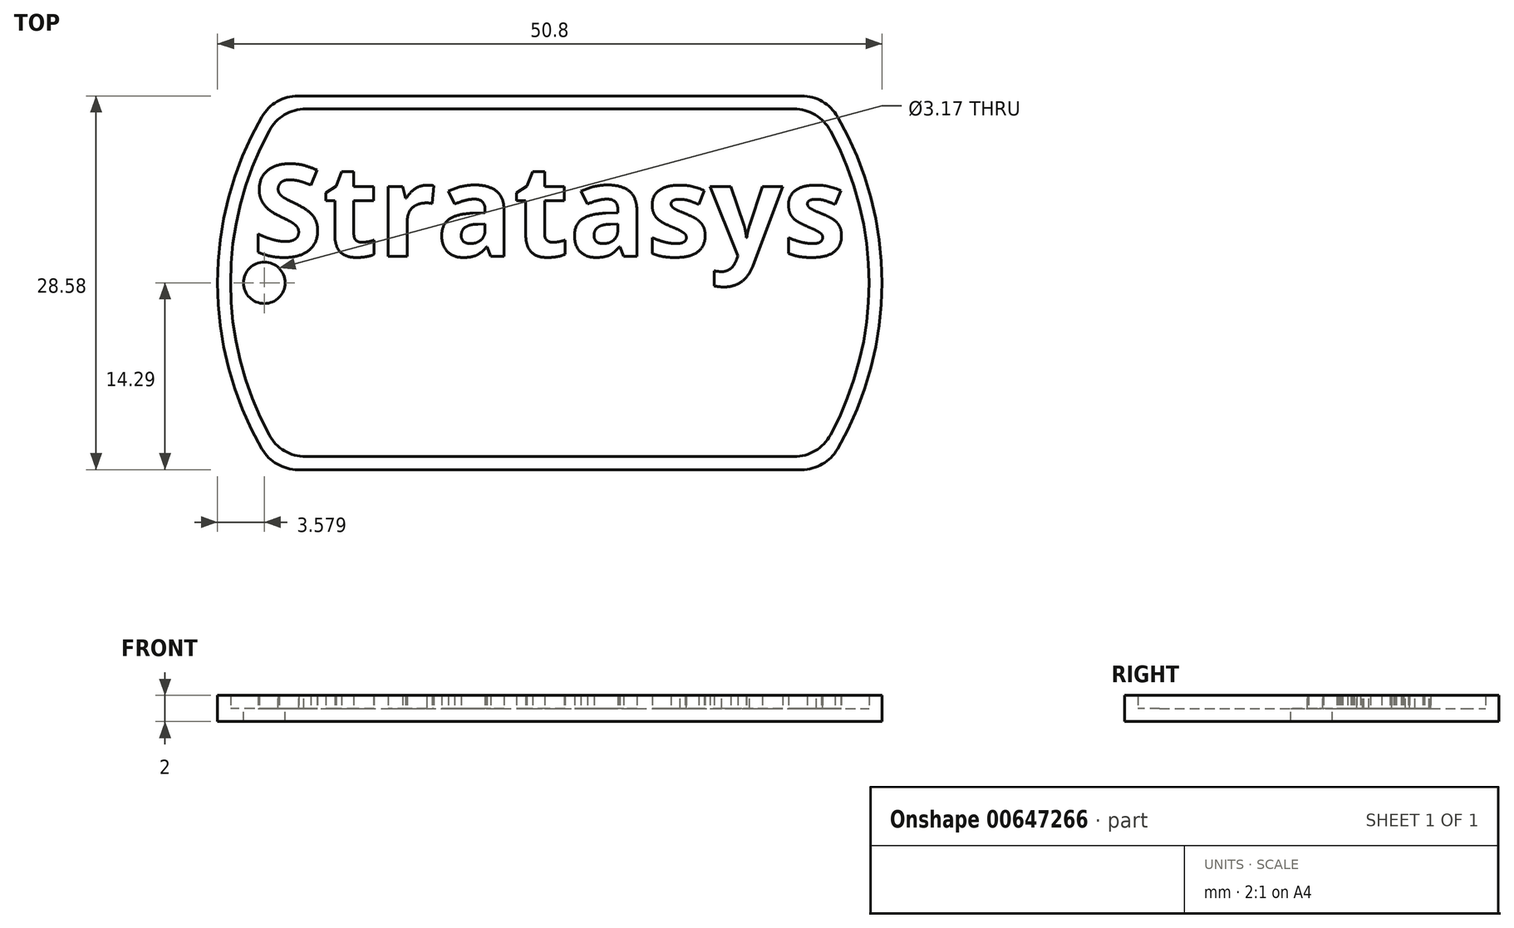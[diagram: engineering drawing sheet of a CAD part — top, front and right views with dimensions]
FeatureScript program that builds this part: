
annotation { "Feature Type Name" : "Feature", "Feature Type Description" : "" }
export const myFeature = defineFeature(function(context is Context, id is Id, definition is map)
    precondition{}
    {
        {
            var Q0;
            Q0=qCreatedBy(makeId("Top.planeOp"),FACE);
            var sketch = newSketch(context, id + "F0", { "sketchPlane" : qUnion([Q0])});
            skArc(sketch, "E0", {"start": v(-22, 12.7) * mm, "mid": v(-25.4, 0) * mm, "end": v(-22, -12.7) * mm});
            skLineSegment(sketch, "E1.top", {"start": v(-19.25, -14.29) * mm, "end": v(19.25, -14.29) * mm});
            skArc(sketch, "E2.trimOffspring", {"start": v(22, -12.7) * mm, "mid": v(25.4, 0) * mm, "end": v(22, 12.7) * mm});
            skLineSegment(sketch, "E3", {"start": v(-19.25, 14.29) * mm, "end": v(19.25, 14.29) * mm});
            skPoint(sketch, "E4.visualSharp", {"position": v(-21, 14.29) * mm});
            skArc(sketch, "E4.filletArc", {"start": v(-19.25, 14.29) * mm, "mid": v(-20.83, 13.86) * mm, "end": v(-22, 12.7) * mm});
            skPoint(sketch, "E5.visualSharp", {"position": v(21, 14.29) * mm});
            skArc(sketch, "E5.filletArc", {"start": v(22, 12.7) * mm, "mid": v(20.83, 13.86) * mm, "end": v(19.25, 14.29) * mm});
            skPoint(sketch, "E6.visualSharp", {"position": v(21, -14.29) * mm});
            skArc(sketch, "E6.filletArc", {"start": v(19.25, -14.29) * mm, "mid": v(20.83, -13.86) * mm, "end": v(22, -12.7) * mm});
            skPoint(sketch, "E7.visualSharp", {"position": v(-21, -14.29) * mm});
            skArc(sketch, "E7.filletArc", {"start": v(-22, -12.7) * mm, "mid": v(-20.83, -13.86) * mm, "end": v(-19.25, -14.29) * mm});
            skSolve(sketch);
        }
        {
            var Q0;
            Q0=makeQuery(id+"F0.imprint","IMPRINT",FACE,{"disambiguationData":[TD([[makeQuery(id+"F0.imprint","IMPRINT",EDGE,{"derivedFrom":sQuery(id+"F0.wireOp",EDGE,"E0")}),1.0]])]});
            extrude(context, id + "F1", {"entities" : qUnion([Q0]), "depth" : 1 * mm, "offsetDistance" : 25.4 * mm});
        }
        {
            var Q0;
            Q0=makeQuery(id+"F1.opExtrude","CAP_FACE",FACE,{"disambiguationData":[OSD([sQuery(id+"F0.wireOp",EDGE,"E0"),sQuery(id+"F0.wireOp",EDGE,"E1.top"),sQuery(id+"F0.wireOp",EDGE,"E2.trimOffspring"),sQuery(id+"F0.wireOp",EDGE,"E3"),sQuery(id+"F0.wireOp",EDGE,"E4.filletArc"),sQuery(id+"F0.wireOp",EDGE,"E5.filletArc"),sQuery(id+"F0.wireOp",EDGE,"E6.filletArc"),sQuery(id+"F0.wireOp",EDGE,"E7.filletArc")])],"isStart":false});
            var sketch = newSketch(context, id + "F2", { "sketchPlane" : qUnion([Q0])});
            skLineSegment(sketch, "E8.0", {"start": v(-18.66, 13.29) * mm, "end": v(18.66, 13.29) * mm});
            skArc(sketch, "E8.1", {"start": v(-21.45, 11.63) * mm, "mid": v(-24.4, 0) * mm, "end": v(-21.45, -11.63) * mm});
            skLineSegment(sketch, "E8.2", {"start": v(-18.66, -13.29) * mm, "end": v(18.66, -13.29) * mm});
            skArc(sketch, "E8.3", {"start": v(21.45, -11.63) * mm, "mid": v(24.4, 0) * mm, "end": v(21.45, 11.63) * mm});
            skPoint(sketch, "E9.visualSharp", {"position": v(-20.46, 13.29) * mm});
            skArc(sketch, "E9.filletArc", {"start": v(-18.66, 13.29) * mm, "mid": v(-20.29, 12.84) * mm, "end": v(-21.45, 11.63) * mm});
            skPoint(sketch, "E10.visualSharp", {"position": v(20.46, 13.29) * mm});
            skArc(sketch, "E10.filletArc", {"start": v(21.45, 11.63) * mm, "mid": v(20.29, 12.84) * mm, "end": v(18.66, 13.29) * mm});
            skPoint(sketch, "E11.visualSharp", {"position": v(20.46, -13.29) * mm});
            skArc(sketch, "E11.filletArc", {"start": v(18.66, -13.29) * mm, "mid": v(20.29, -12.84) * mm, "end": v(21.45, -11.63) * mm});
            skPoint(sketch, "E12.visualSharp", {"position": v(-20.46, -13.29) * mm});
            skArc(sketch, "E12.filletArc", {"start": v(-21.45, -11.63) * mm, "mid": v(-20.29, -12.84) * mm, "end": v(-18.66, -13.29) * mm});
            skLineSegment(sketch, "E13.0", {"start": v(-19.25, 14.29) * mm, "end": v(19.25, 14.29) * mm});
            skArc(sketch, "E13.1", {"start": v(-22, 12.7) * mm, "mid": v(-25.4, 0) * mm, "end": v(-22, -12.7) * mm});
            skLineSegment(sketch, "E13.2", {"start": v(-19.25, -14.29) * mm, "end": v(19.25, -14.29) * mm});
            skArc(sketch, "E13.3", {"start": v(22, -12.7) * mm, "mid": v(25.4, 0) * mm, "end": v(22, 12.7) * mm});
            skPoint(sketch, "E14.visualSharp", {"position": v(-21, -14.29) * mm});
            skArc(sketch, "E14.filletArc", {"start": v(-22, -12.7) * mm, "mid": v(-20.83, -13.86) * mm, "end": v(-19.25, -14.29) * mm});
            skPoint(sketch, "E15.visualSharp", {"position": v(21, -14.29) * mm});
            skArc(sketch, "E15.filletArc", {"start": v(19.25, -14.29) * mm, "mid": v(20.83, -13.86) * mm, "end": v(22, -12.7) * mm});
            skPoint(sketch, "E16.visualSharp", {"position": v(21, 14.29) * mm});
            skArc(sketch, "E16.filletArc", {"start": v(22, 12.7) * mm, "mid": v(20.83, 13.86) * mm, "end": v(19.25, 14.29) * mm});
            skPoint(sketch, "E17.visualSharp", {"position": v(-21, 14.29) * mm});
            skArc(sketch, "E17.filletArc", {"start": v(-19.25, 14.29) * mm, "mid": v(-20.83, 13.86) * mm, "end": v(-22, 12.7) * mm});
            skSolve(sketch);
        }
        {
            var Q0;
            Q0=makeQuery(id+"F2.imprint","IMPRINT",FACE,{"disambiguationData":[TD([[makeQuery(id+"F2.imprint","IMPRINT",EDGE,{"derivedFrom":sQuery(id+"F2.wireOp",EDGE,"E8.0")}),1.0]])]});
            extrude(context, id + "F3", {"entities" : qUnion([Q0]), "operationType" : NewBodyOperationType.ADD, "depth" : 1 * mm, "offsetDistance" : 25.4 * mm});
        }
        {
            var Q0;
            Q0=makeQuery(id+"F1.opExtrude","CAP_FACE",FACE,{"disambiguationData":[OSD([sQuery(id+"F0.wireOp",EDGE,"E0"),sQuery(id+"F0.wireOp",EDGE,"E1.top"),sQuery(id+"F0.wireOp",EDGE,"E2.trimOffspring"),sQuery(id+"F0.wireOp",EDGE,"E3"),sQuery(id+"F0.wireOp",EDGE,"E4.filletArc"),sQuery(id+"F0.wireOp",EDGE,"E5.filletArc"),sQuery(id+"F0.wireOp",EDGE,"E6.filletArc"),sQuery(id+"F0.wireOp",EDGE,"E7.filletArc")])],"isStart":false});
            var sketch = newSketch(context, id + "F4", { "sketchPlane" : qUnion([Q0])});
            skCircle(sketch, "E18", {"center": v(-21.82, 0) * mm, "radius": 1.59 * mm});
            skSolve(sketch);
        }
        {
            var Q0;
            Q0=makeQuery(id+"F4.imprint","IMPRINT",FACE,{"disambiguationData":[TD([[makeQuery(id+"F4.imprint","IMPRINT",EDGE,{"derivedFrom":sQuery(id+"F4.wireOp",EDGE,"E18")}),1.0]])]});
            extrude(context, id + "F5", {"entities" : qUnion([Q0]), "operationType" : NewBodyOperationType.REMOVE, "oppositeDirection" : true, "depth" : 1 * mm, "offsetDistance" : 25.4 * mm});
        }
        {
            var Q0;
            Q0=makeQuery(id+"F1.opExtrude","CAP_FACE",FACE,{"disambiguationData":[OSD([sQuery(id+"F0.wireOp",EDGE,"E0"),sQuery(id+"F0.wireOp",EDGE,"E1.top"),sQuery(id+"F0.wireOp",EDGE,"E2.trimOffspring"),sQuery(id+"F0.wireOp",EDGE,"E3"),sQuery(id+"F0.wireOp",EDGE,"E4.filletArc"),sQuery(id+"F0.wireOp",EDGE,"E5.filletArc"),sQuery(id+"F0.wireOp",EDGE,"E6.filletArc"),sQuery(id+"F0.wireOp",EDGE,"E7.filletArc")])],"isStart":false});
            var sketch = newSketch(context, id + "F6", { "sketchPlane" : qUnion([Q0])});
            skText(sketch, "E19", { "text": "Stratasys", "fontName": "OpenSans-Bold.ttf"});
            const initialGuessF6  = {"E19": [-0.02274, 0.00203, 1, 0, 0.00704]};
            skSetInitialGuess(sketch, initialGuessF6);
            skSolve(sketch);
        }
        {
            var Q0;
            Q0 = qSketchRegion(id + "F6", true);
            extrude(context, id + "F7", {"entities" : qUnion([Q0]), "operationType" : NewBodyOperationType.ADD, "depth" : 1 * mm, "offsetDistance" : 25.4 * mm});
        }
    });
